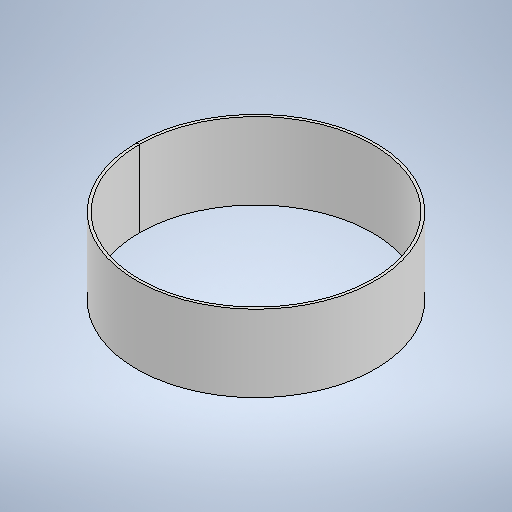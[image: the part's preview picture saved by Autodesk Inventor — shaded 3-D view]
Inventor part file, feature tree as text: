
AUTODESK INVENTOR PART (.ipt)
format: ipt  version: 2025.1 (Build 291241020, 241B)  size: 278,528 bytes
history: native  units: mm
features: sketch x2, revolve x1, extrude x1, other x1
ambient origin geometry x8: Origin, YZ Plane, XZ Plane, XY Plane, X Axis, Y Axis, Z Axis, Center Point
bodies: Solid1 (feature_tree)
feature tree (5):
  revolve  "Revolution1"  [1 undecoded]
  extrude  "Extrusion1"  Depth=6.0mm
  sketch  "Sketch1"  dims[d1=6.0mm d3=6.0mm d5=120.0mm]
  sketch  "Sketch2"  dims[d6=62.8144mm d7=6.0mm d8=50.0mm d9=1212.0mm d10=0.0mm d11=0.0mm d12=530.0mm]
  other  "Definition1"
note: 1 required parameter value undecoded (feature->parameter linkage not recoverable at this tier; creation-order binding heuristic only, values carry confidence <= 0.55)
